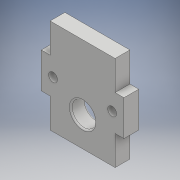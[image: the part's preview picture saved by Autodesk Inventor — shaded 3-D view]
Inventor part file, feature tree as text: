
AUTODESK INVENTOR PART (.ipt)
format: ipt  version: 2018 (Build 220112000, 112)  size: 139,264 bytes
history: native  units: mm
features: extrude x2, sketch x2, fillet x1
ambient origin geometry x8: Origin, YZ Plane, XZ Plane, XY Plane, X Axis, Y Axis, Z Axis, Center Point
bodies: Body1 (feature_tree)
feature tree (5):
  extrude  "Extrusión2"  Depth=10.0mm
  fillet  "Empalme1"  Radius=3.0mm
  extrude  "Extrusión3"  Depth=10.0mm
  sketch  "Boceto1"  dims[d0=22.0mm d1=10.0mm d2=3.0mm]
  sketch  "Boceto2"  dims[d3=12.0mm d4=10.0mm d5=10.0mm d6=3.0mm d10=8.0mm d11=5.0mm d12=0.0mm d13=0.5mm d14=4.0mm d15=4.0mm d16=3.0mm d17=3.0mm d18=5.0mm d19=0.0mm]
